# Revit family: DRR30980RAP
name_source: partatom
category: Specialty Equipment
revit_build: Autodesk Revit MEP 2014 (Build: 20130308_1515(x64)
units: mm (PartAtom-declared; Revit-internal decimal feet)

## types (1)
- DRR30980RAP
    Annual Energy Consumption = 280 kWy/year
    Crisper Drawers = 2 ea
    Current (A) = 3
    Dedicated Evaporator & Compressor System = Yes
    Deodorizing Filter = Yes
    Depth = 25"
    Description = 30-INCH REFRIGERATOR COLUMN, RIGHT-HINGE
    Door = Stainless Steel
    Door Bins = 4 ea
    Door Open Alarm = Yes
    Door Swing = Right
    ENERGY STAR® Qualified = Yes
    Frequency (Hz) = 60
    FreshZone™ Drawer = Yes - Cheese (37°F) / Cold Drinks (33°F) / Meat (29°F)
    Full Extension Drawers at 90º Door Opening Angle = Yes
    Full Width Shelves = 4 ea
    Handle = Stainless Steel
    Height = 83 3/8"
    Interior Material = SteelCool™ Stainless Steel Interior
    Internal Water Dispenser = Yes
    Lighting = 3DLighting™
    Manufacturer = Dacor
    Model = DRR30980RAP
    Panel Ready = Yes
    Plug Type = 120 V, 3 Prong
    Power Cool = Yes
    Power Cord Length (in.) = 78 3/4"
    Precise Cooling = Yes
    Push-To-Open™ Door Assist = Yes
    Refrigerator = 34°F (1°C) to 44°F (7°C)
    Refrigerator - Power Cool = 34°F (1°C)
    Refrigerator Gross Capacity (cu.ft.) = 17.8 cu. ft.
    Shelf Material = Tempered, Metal Trim, Spill-Proof
    Special Modes = Sabbath Mode
    Support = Plastic-Black
    Total Unit Gross Capacity (cu.ft.) - AHAM = 17.8 cu. ft.
    Unit = Stainless Steel
    Volts (V) = 115
    Width = 29 3/4"
    iQ RemoteView™ Camera = Yes (2 ea)

## geometry (parser evidence)
native form markers: Sweep x1
no freeform markers — native parametric forms only
